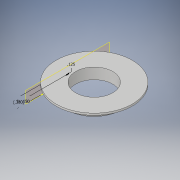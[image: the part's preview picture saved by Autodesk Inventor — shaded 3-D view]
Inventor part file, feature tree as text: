
AUTODESK INVENTOR PART (.ipt)
format: ipt  version: 2019 (Build 230136000, 136)  size: 126,976 bytes
history: native  units: in
note: dims shown in document units (in); Inventor stores cm internally (conversion verified against a paired STEP export)
features: sketch x3, projected_geometry x2, revolve x1, extrude x1
ambient origin geometry x8: Origin, YZ Plane, XZ Plane, XY Plane, X Axis, Y Axis, Z Axis, Center Point
bodies: Solid1 (feature_tree)
feature tree (7):
  revolve  "Revolution1"  [1 undecoded]
  extrude  "Extrusion1"  Depth=1.22in
  sketch  "Sketch3"  dims[d23=0.36in d24=0.0in d25=0.3in d26=0.15in d34=0.125in]
  sketch  "Sketch1"  dims[d1=1.75in d7=0.875in]
  sketch  "Sketch2"  dims[d8=180.0deg d22=1.22in]
  projected_geometry  "Projected Loop1"
  projected_geometry  "Projected Loop2"
note: 1 required parameter value undecoded (feature->parameter linkage not recoverable at this tier; creation-order binding heuristic only, values carry confidence <= 0.55)
